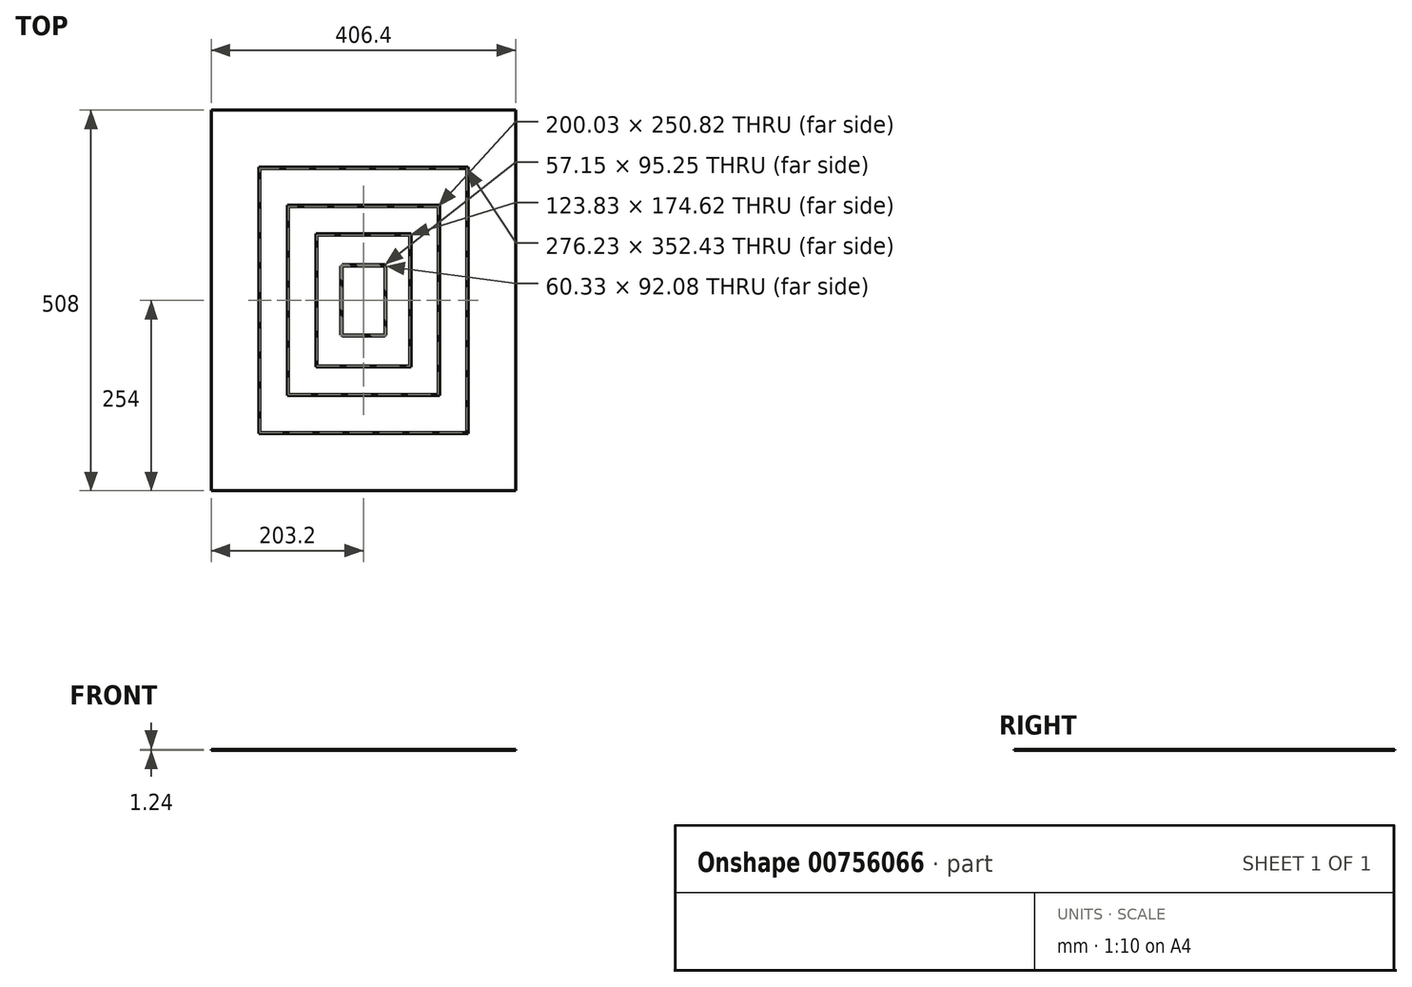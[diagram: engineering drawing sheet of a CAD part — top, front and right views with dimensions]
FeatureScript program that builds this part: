
annotation { "Feature Type Name" : "Feature", "Feature Type Description" : "" }
export const myFeature = defineFeature(function(context is Context, id is Id, definition is map)
    precondition{}
    {
        {
            var Q0;
            Q0=qCreatedBy(makeId("Top.planeOp"),FACE);
            var sketch = newSketch(context, id + "F0", { "sketchPlane" : qUnion([Q0])});
            skLineSegment(sketch, "E0.bottom", {"start": v(203.2, -254) * mm, "end": v(-203.2, -254) * mm});
            skLineSegment(sketch, "E0.top", {"start": v(203.2, 254) * mm, "end": v(-203.2, 254) * mm});
            skLineSegment(sketch, "E0.left", {"start": v(203.2, -254) * mm, "end": v(203.2, 254) * mm});
            skLineSegment(sketch, "E0.right", {"start": v(-203.2, -254) * mm, "end": v(-203.2, 254) * mm});
            skPoint(sketch, "E0.middle", {"position": v(0, 0) * mm});
            skLineSegment(sketch, "E1.bottom", {"start": v(138.11, -176.21) * mm, "end": v(-138.11, -176.21) * mm});
            skLineSegment(sketch, "E1.top", {"start": v(138.11, 176.21) * mm, "end": v(-138.11, 176.21) * mm});
            skLineSegment(sketch, "E1.left", {"start": v(138.11, -176.21) * mm, "end": v(138.11, 176.21) * mm});
            skLineSegment(sketch, "E1.right", {"start": v(-138.11, -176.21) * mm, "end": v(-138.11, 176.21) * mm});
            skSolve(sketch);
        }
        {
            var Q0;
            Q0=qCreatedBy(makeId("Top.planeOp"),FACE);
            var sketch = newSketch(context, id + "F1", { "sketchPlane" : qUnion([Q0])});
            skLineSegment(sketch, "E2.bottom", {"start": v(139.7, -177.8) * mm, "end": v(-139.7, -177.8) * mm});
            skLineSegment(sketch, "E2.top", {"start": v(139.7, 177.8) * mm, "end": v(-139.7, 177.8) * mm});
            skLineSegment(sketch, "E2.left", {"start": v(139.7, -177.8) * mm, "end": v(139.7, 177.8) * mm});
            skLineSegment(sketch, "E2.right", {"start": v(-139.7, -177.8) * mm, "end": v(-139.7, 177.8) * mm});
            skPoint(sketch, "E2.middle", {"position": v(0, 0) * mm});
            skLineSegment(sketch, "E3.bottom", {"start": v(100.01, -125.41) * mm, "end": v(-100.01, -125.41) * mm});
            skLineSegment(sketch, "E3.top", {"start": v(100.01, 125.41) * mm, "end": v(-100.01, 125.41) * mm});
            skLineSegment(sketch, "E3.left", {"start": v(100.01, -125.41) * mm, "end": v(100.01, 125.41) * mm});
            skLineSegment(sketch, "E3.right", {"start": v(-100.01, -125.41) * mm, "end": v(-100.01, 125.41) * mm});
            skSolve(sketch);
        }
        {
            var Q0;
            Q0=qCreatedBy(makeId("Top.planeOp"),FACE);
            var sketch = newSketch(context, id + "F2", { "sketchPlane" : qUnion([Q0])});
            skLineSegment(sketch, "E4.bottom", {"start": v(101.6, -127) * mm, "end": v(-101.6, -127) * mm});
            skLineSegment(sketch, "E4.top", {"start": v(101.6, 127) * mm, "end": v(-101.6, 127) * mm});
            skLineSegment(sketch, "E4.left", {"start": v(101.6, -127) * mm, "end": v(101.6, 127) * mm});
            skLineSegment(sketch, "E4.right", {"start": v(-101.6, -127) * mm, "end": v(-101.6, 127) * mm});
            skPoint(sketch, "E4.middle", {"position": v(0, 0) * mm});
            skLineSegment(sketch, "E5.bottom", {"start": v(61.91, -87.31) * mm, "end": v(-61.91, -87.31) * mm});
            skLineSegment(sketch, "E5.top", {"start": v(61.91, 87.31) * mm, "end": v(-61.91, 87.31) * mm});
            skLineSegment(sketch, "E5.left", {"start": v(61.91, -87.31) * mm, "end": v(61.91, 87.31) * mm});
            skLineSegment(sketch, "E5.right", {"start": v(-61.91, -87.31) * mm, "end": v(-61.91, 87.31) * mm});
            skSolve(sketch);
        }
        {
            var Q0;
            Q0=qCreatedBy(makeId("Top.planeOp"),FACE);
            var sketch = newSketch(context, id + "F3", { "sketchPlane" : qUnion([Q0])});
            skLineSegment(sketch, "E6.bottom", {"start": v(63.5, -88.9) * mm, "end": v(-63.5, -88.9) * mm});
            skLineSegment(sketch, "E6.top", {"start": v(63.5, 88.9) * mm, "end": v(-63.5, 88.9) * mm});
            skLineSegment(sketch, "E6.left", {"start": v(63.5, -88.9) * mm, "end": v(63.5, 88.9) * mm});
            skLineSegment(sketch, "E6.right", {"start": v(-63.5, -88.9) * mm, "end": v(-63.5, 88.9) * mm});
            skPoint(sketch, "E6.middle", {"position": v(0, 0) * mm});
            skLineSegment(sketch, "E7.bottom", {"start": v(28.57, -47.62) * mm, "end": v(-28.58, -47.63) * mm});
            skLineSegment(sketch, "E7.top", {"start": v(28.58, 47.63) * mm, "end": v(-28.57, 47.62) * mm});
            skLineSegment(sketch, "E7.left", {"start": v(28.57, -47.62) * mm, "end": v(28.58, 47.63) * mm});
            skLineSegment(sketch, "E7.right", {"start": v(-28.58, -47.63) * mm, "end": v(-28.57, 47.62) * mm});
            skSolve(sketch);
        }
        {
            var Q0;
            Q0=qCreatedBy(makeId("Top.planeOp"),FACE);
            var sketch = newSketch(context, id + "F4", { "sketchPlane" : qUnion([Q0])});
            skLineSegment(sketch, "E8.bottom", {"start": v(63.5, -88.9) * mm, "end": v(-63.5, -88.9) * mm});
            skLineSegment(sketch, "E8.top", {"start": v(63.5, 88.9) * mm, "end": v(-63.5, 88.9) * mm});
            skLineSegment(sketch, "E8.left", {"start": v(63.5, -88.9) * mm, "end": v(63.5, 88.9) * mm});
            skLineSegment(sketch, "E8.right", {"start": v(-63.5, -88.9) * mm, "end": v(-63.5, 88.9) * mm});
            skPoint(sketch, "E8.middle", {"position": v(0, 0) * mm});
            skLineSegment(sketch, "E9.bottom", {"start": v(30.16, -46.04) * mm, "end": v(-30.16, -46.04) * mm});
            skLineSegment(sketch, "E9.top", {"start": v(30.16, 46.04) * mm, "end": v(-30.16, 46.04) * mm});
            skLineSegment(sketch, "E9.left", {"start": v(30.16, -46.04) * mm, "end": v(30.16, 46.04) * mm});
            skLineSegment(sketch, "E9.right", {"start": v(-30.16, -46.04) * mm, "end": v(-30.16, 46.04) * mm});
            skSolve(sketch);
        }
        {
            var Q0;
            Q0 = qSketchRegion(id + "F0", true);
            var Q1;
            Q1 = qSketchRegion(id + "F1", true);
            var Q2;
            Q2 = qSketchRegion(id + "F2", true);
            var Q3;
            Q3 = qSketchRegion(id + "F4", true);
            var Q4;
            Q4 = qSketchRegion(id + "F3", true);
            extrude(context, id + "F5", {"entities" : qUnion([Q0, Q1, Q2, Q3, Q4]), "depth" : 1.24 * mm, "offsetDistance" : 25.4 * mm});
        }
    });
